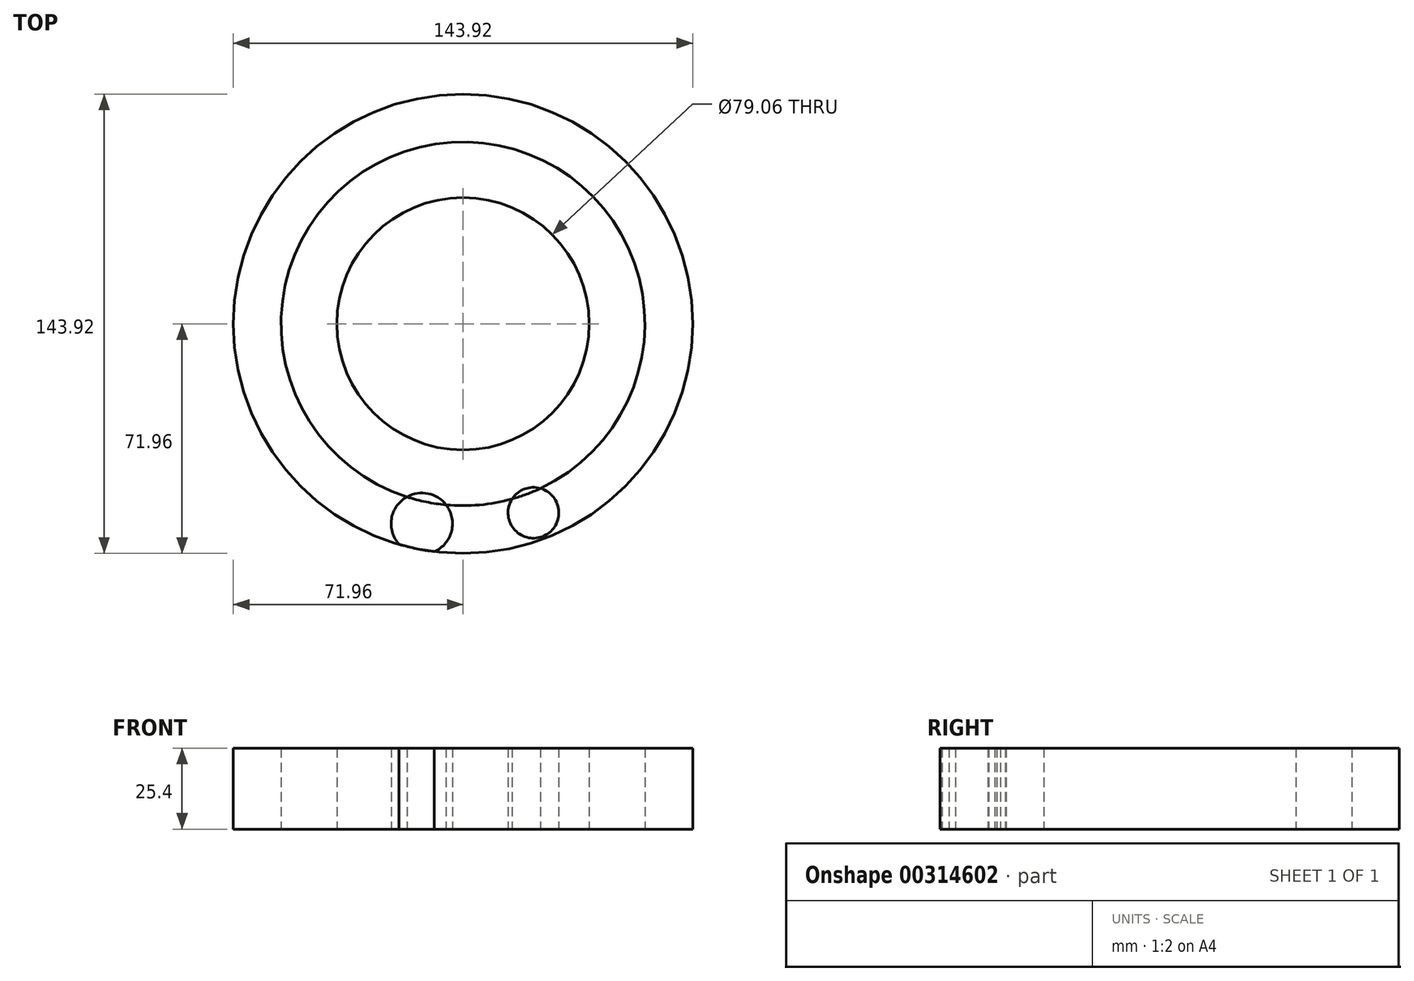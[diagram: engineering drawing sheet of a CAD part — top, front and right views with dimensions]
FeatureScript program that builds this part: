
annotation { "Feature Type Name" : "Feature", "Feature Type Description" : "" }
export const myFeature = defineFeature(function(context is Context, id is Id, definition is map)
    precondition{}
    {
        {
            var Q0;
            Q0=qCreatedBy(makeId("Top.planeOp"),FACE);
            var sketch = newSketch(context, id + "F0", { "sketchPlane" : qUnion([Q0])});
            skCircle(sketch, "E0", {"center": v(0, 0) * mm, "radius": 71.96 * mm});
            skCircle(sketch, "E1", {"center": v(0, 0) * mm, "radius": 57 * mm});
            skCircle(sketch, "E2", {"center": v(0, 0) * mm, "radius": 39.53 * mm});
            skSolve(sketch);
        }
        {
            var Q0;
            Q0=makeQuery(id+"F0.imprint","IMPRINT",FACE,{"disambiguationData":[TD([[makeQuery(id+"F0.imprint","IMPRINT",EDGE,{"derivedFrom":sQuery(id+"F0.wireOp",EDGE,"E0")}),1.0]])]});
            var sketch = newSketch(context, id + "F1", { "sketchPlane" : qUnion([Q0])});
            skCircle(sketch, "E3", {"center": v(-12.9, -62.64) * mm, "radius": 9.62 * mm});
            skCircle(sketch, "E4", {"center": v(22.08, -59.23) * mm, "radius": 7.96 * mm});
            skSolve(sketch);
        }
        {
            var Q0;
            {var subQ0=sQuery(id+"F1.wireOp",EDGE,"E3");var subQ1=makeQuery(id+"F0.imprint","IMPRINT",EDGE,{"derivedFrom":sQuery(id+"F0.wireOp",EDGE,"E0")});var subQ2=makeQuery(id+"F1.imprint","INTERSECT",VERTEX,{"disambiguationData":[OD(0.0)],"derivedFrom":[subQ1,subQ0]});Q0=makeQuery(id+"F1.imprint","IMPRINT",FACE,{"disambiguationData":[TD([[makeQuery(id+"F1.imprint","IMPRINT",EDGE,{"disambiguationData":[TD([[subQ2,1.0]])],"derivedFrom":subQ0}),1.0]])]});}
            var Q1;
            {var subQ0=sQuery(id+"F1.wireOp",EDGE,"E4");var subQ1=makeQuery(id+"F0.imprint","IMPRINT",EDGE,{"derivedFrom":sQuery(id+"F0.wireOp",EDGE,"E1")});var subQ2=makeQuery(id+"F1.imprint","INTERSECT",VERTEX,{"disambiguationData":[OD(0.0)],"derivedFrom":[subQ1,subQ0]});Q1=makeQuery(id+"F1.imprint","IMPRINT",FACE,{"disambiguationData":[TD([[makeQuery(id+"F1.imprint","IMPRINT",EDGE,{"disambiguationData":[TD([[subQ2,1.0]])],"derivedFrom":subQ0}),1.0]])]});}
            var Q2;
            {var subQ0=sQuery(id+"F1.wireOp",EDGE,"E3");var subQ1=makeQuery(id+"F0.imprint","IMPRINT",EDGE,{"derivedFrom":sQuery(id+"F0.wireOp",EDGE,"E1")});var subQ2=makeQuery(id+"F1.imprint","INTERSECT",VERTEX,{"disambiguationData":[OD(0.0)],"derivedFrom":[subQ1,subQ0]});Q2=makeQuery(id+"F1.imprint","IMPRINT",FACE,{"disambiguationData":[TD([[makeQuery(id+"F1.imprint","IMPRINT",EDGE,{"disambiguationData":[TD([[subQ2,1.0]])],"derivedFrom":subQ0}),-1.0]])]});}
            var Q3;
            Q3=makeQuery(id+"F0.imprint","IMPRINT",FACE,{"disambiguationData":[TD([[makeQuery(id+"F0.imprint","IMPRINT",EDGE,{"derivedFrom":sQuery(id+"F0.wireOp",EDGE,"E0")}),1.0]])]});
            var Q4;
            Q4=makeQuery(id+"F0.imprint","IMPRINT",FACE,{"disambiguationData":[TD([[makeQuery(id+"F0.imprint","IMPRINT",EDGE,{"derivedFrom":sQuery(id+"F0.wireOp",EDGE,"E1")}),1.0]])]});
            extrude(context, id + "F2", {"entities" : qUnion([Q0, Q1, Q2, Q3, Q4]), "depth" : 25.4 * mm});
        }
        {
            var Q0;
            Q0=makeQuery(id+"F2.opExtrude","SWEPT_BODY",BODY,{"disambiguationData":[OSD([sQuery(id+"F0.wireOp",EDGE,"E0"),sQuery(id+"F0.wireOp",EDGE,"E1"),sQuery(id+"F1.wireOp",EDGE,"E3")])]});
            var Q1;
            {var subQ0=sQuery(id+"F0.wireOp",EDGE,"E0");Q1=makeQuery(id+"F2.opExtrude","CAP_EDGE",EDGE,{"disambiguationData":[OSD([subQ0]),TDD([makeQuery(id+"F0.imprint","IMPRINT",EDGE,{"derivedFrom":subQ0})])],"isStart":false});}
            circularPattern(context, id + "F3", {"entities" : qUnion([Q0]), "axis" : qUnion([Q1]), "angle" : 360 * degree, "instanceCount" : 13});
        }
    });
